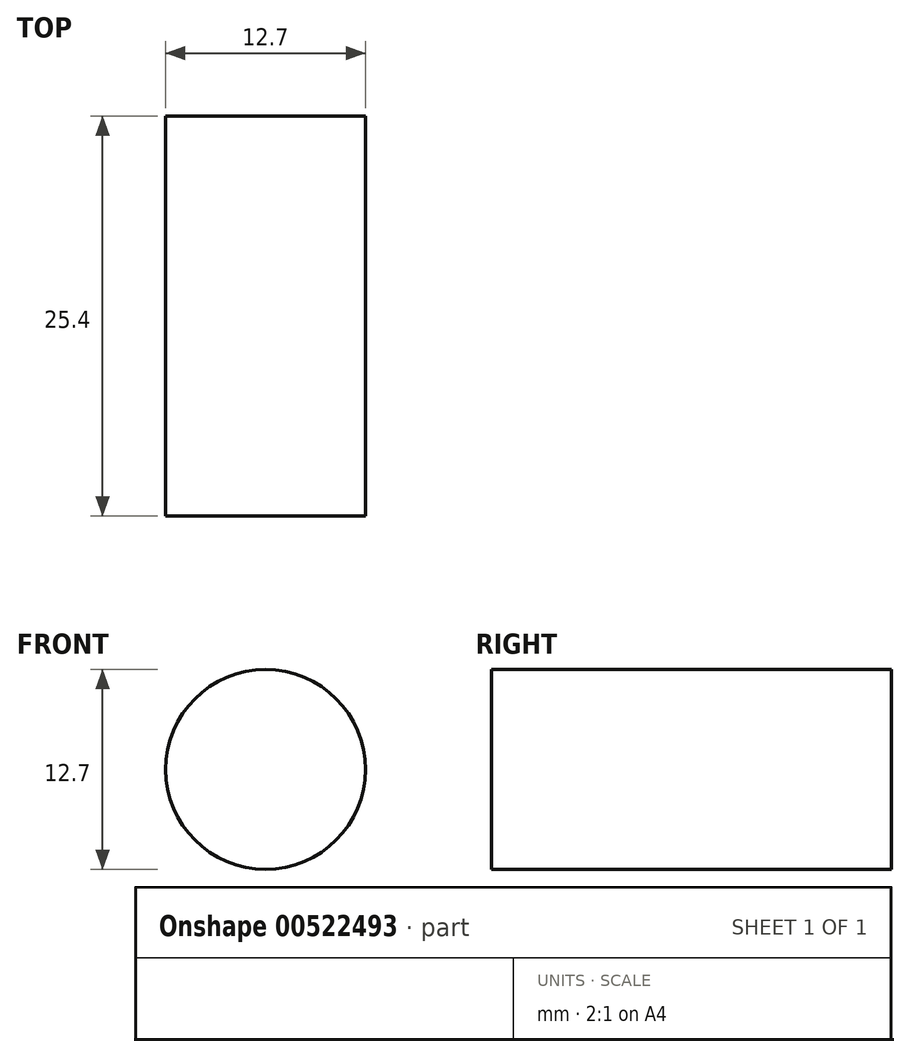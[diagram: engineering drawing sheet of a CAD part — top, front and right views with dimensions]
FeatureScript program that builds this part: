
annotation { "Feature Type Name" : "Feature", "Feature Type Description" : "" }
export const myFeature = defineFeature(function(context is Context, id is Id, definition is map)
    precondition{}
    {
        {
            var Q0;
            Q0=qCreatedBy(makeId("Front.planeOp"),FACE);
            var sketch = newSketch(context, id + "F0", { "sketchPlane" : qUnion([Q0])});
            skCircle(sketch, "E0", {"center": v(0, 0) * mm, "radius": 6.35 * mm});
            skSolve(sketch);
        }
        {
            var Q0;
            Q0 = qSketchRegion(id + "F0", true);
            extrude(context, id + "F1", {"entities" : qUnion([Q0]), "depth" : 25.4 * mm, "offsetDistance" : 25.4 * mm});
        }
    });
